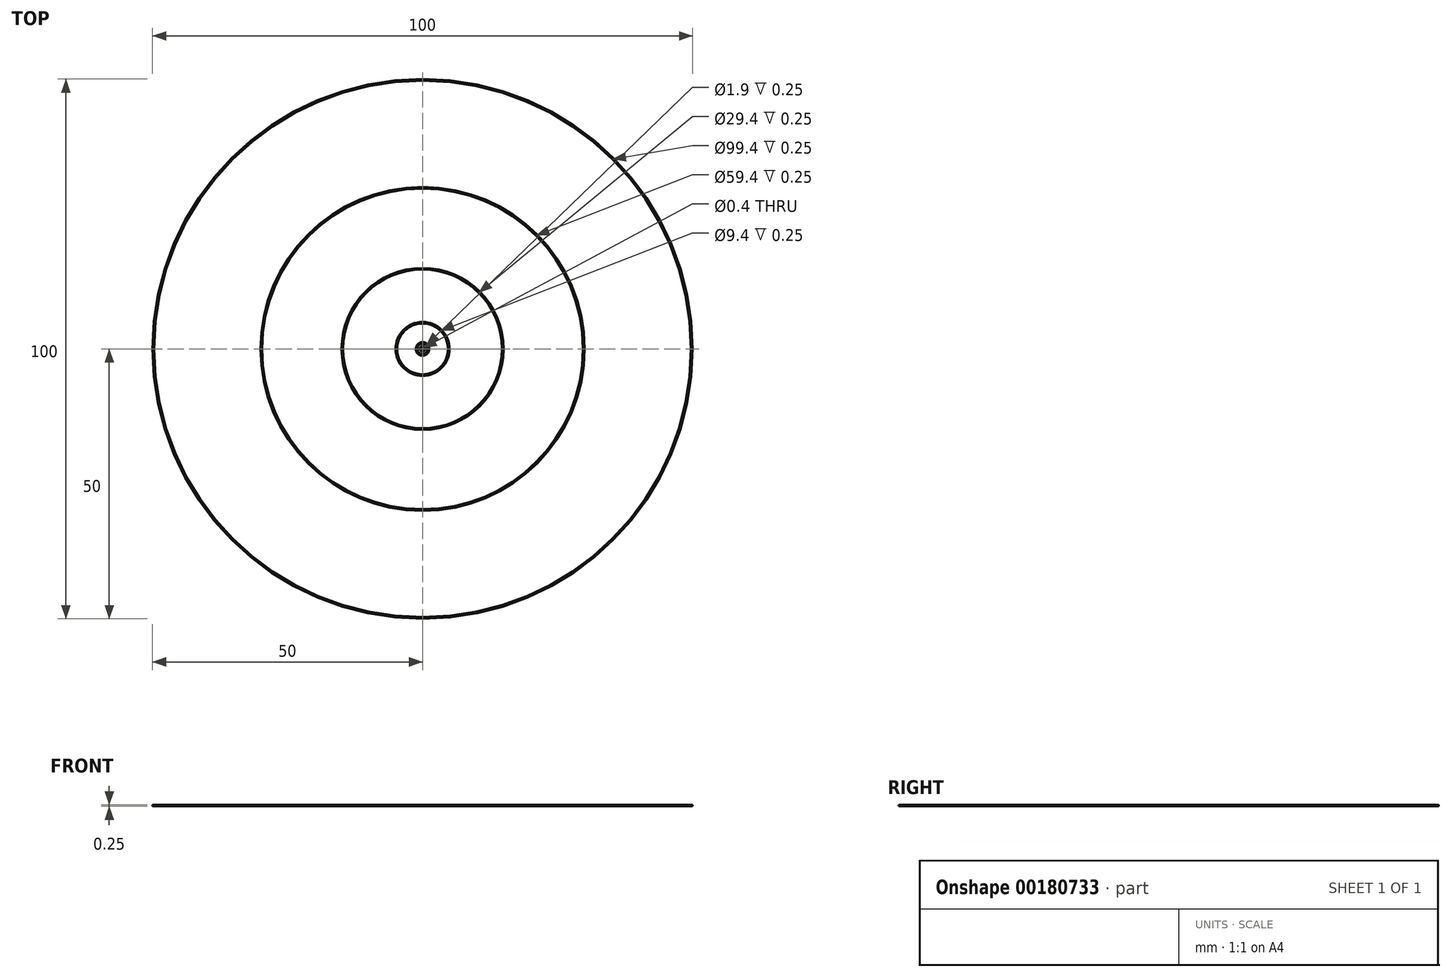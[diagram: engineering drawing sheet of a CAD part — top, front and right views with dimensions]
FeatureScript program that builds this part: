
annotation { "Feature Type Name" : "Feature", "Feature Type Description" : "" }
export const myFeature = defineFeature(function(context is Context, id is Id, definition is map)
    precondition{}
    {
        {
            var Q0;
            Q0=qCreatedBy(makeId("Top.planeOp"),FACE);
            var sketch = newSketch(context, id + "F0", { "sketchPlane" : qUnion([Q0])});
            skCircle(sketch, "E0", {"center": v(0, 0) * mm, "radius": 30 * mm});
            skCircle(sketch, "E1", {"center": v(0, 0) * mm, "radius": 29.7 * mm});
            skCircle(sketch, "E2", {"center": v(0, 0) * mm, "radius": 15 * mm});
            skCircle(sketch, "E3", {"center": v(0, 0) * mm, "radius": 14.7 * mm});
            skCircle(sketch, "E4", {"center": v(0, 0) * mm, "radius": 5 * mm});
            skCircle(sketch, "E5", {"center": v(0, 0) * mm, "radius": 4.7 * mm});
            skCircle(sketch, "E6", {"center": v(0, 0) * mm, "radius": 1.25 * mm});
            skCircle(sketch, "E7", {"center": v(0, 0) * mm, "radius": 0.95 * mm});
            skCircle(sketch, "E8", {"center": v(0, 0) * mm, "radius": 0.5 * mm});
            skCircle(sketch, "E9", {"center": v(0, 0) * mm, "radius": 0.2 * mm});
            skCircle(sketch, "E10", {"center": v(0, 0) * mm, "radius": 50 * mm});
            skCircle(sketch, "E11.0", {"center": v(0, 0) * mm, "radius": 49.7 * mm});
            skSolve(sketch);
        }
        {
            var Q0;
            Q0=makeQuery(id+"F0.imprint","IMPRINT",FACE,{"disambiguationData":[TD([[makeQuery(id+"F0.imprint","IMPRINT",EDGE,{"derivedFrom":sQuery(id+"F0.wireOp",EDGE,"E0")}),1.0]])]});
            var Q1;
            Q1=makeQuery(id+"F0.imprint","IMPRINT",FACE,{"disambiguationData":[TD([[makeQuery(id+"F0.imprint","IMPRINT",EDGE,{"derivedFrom":sQuery(id+"F0.wireOp",EDGE,"E2")}),1.0]])]});
            var Q2;
            Q2=makeQuery(id+"F0.imprint","IMPRINT",FACE,{"disambiguationData":[TD([[makeQuery(id+"F0.imprint","IMPRINT",EDGE,{"derivedFrom":sQuery(id+"F0.wireOp",EDGE,"E4")}),1.0]])]});
            var Q3;
            Q3=makeQuery(id+"F0.imprint","IMPRINT",FACE,{"disambiguationData":[TD([[makeQuery(id+"F0.imprint","IMPRINT",EDGE,{"derivedFrom":sQuery(id+"F0.wireOp",EDGE,"E6")}),1.0]])]});
            var Q4;
            Q4=makeQuery(id+"F0.imprint","IMPRINT",FACE,{"disambiguationData":[TD([[makeQuery(id+"F0.imprint","IMPRINT",EDGE,{"derivedFrom":sQuery(id+"F0.wireOp",EDGE,"E8")}),1.0]])]});
            var Q5;
            Q5=makeQuery(id+"F0.imprint","IMPRINT",FACE,{"disambiguationData":[TD([[makeQuery(id+"F0.imprint","IMPRINT",EDGE,{"derivedFrom":sQuery(id+"F0.wireOp",EDGE,"E10")}),1.0]])]});
            extrude(context, id + "F1", {"entities" : qUnion([Q0, Q1, Q2, Q3, Q4, Q5]), "depth" : .25 * mm});
        }
    });
